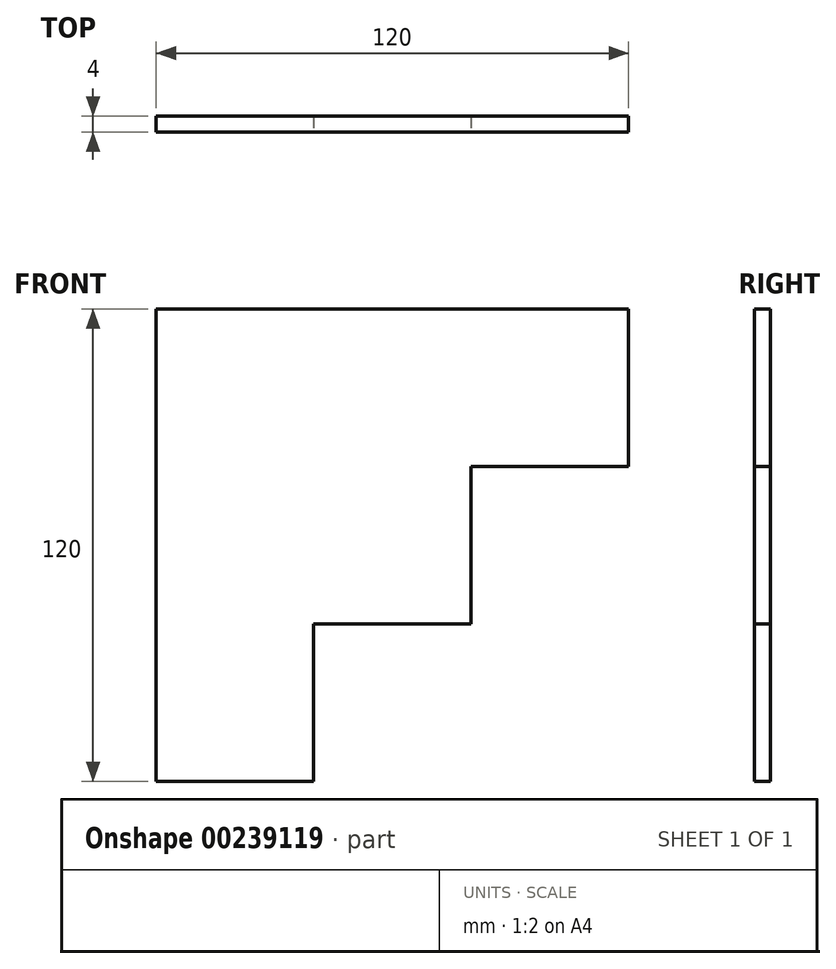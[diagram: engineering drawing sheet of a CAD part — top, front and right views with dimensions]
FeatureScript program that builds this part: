
annotation { "Feature Type Name" : "Feature", "Feature Type Description" : "" }
export const myFeature = defineFeature(function(context is Context, id is Id, definition is map)
    precondition{}
    {
        {
            assignVariable(context, id + "F0", {"name" : "v", "anyValue" : 4});
        }
        {
            var Q0;
            Q0=qCreatedBy(makeId("Front.planeOp"),FACE);
            var sketch = newSketch(context, id + "F1", { "sketchPlane" : qUnion([Q0])});
            skLineSegment(sketch, "E0.bottom", {"start": v(60, 60) * mm, "end": v(-60, 60) * mm});
            skLineSegment(sketch, "E0.top", {"start": v(60, -60) * mm, "end": v(-60, -60) * mm});
            skLineSegment(sketch, "E0.left", {"start": v(60, 60) * mm, "end": v(60, -60) * mm});
            skLineSegment(sketch, "E0.right", {"start": v(-60, 60) * mm, "end": v(-60, -60) * mm});
            skPoint(sketch, "E0.middle", {"position": v(0, 0) * mm});
            skSolve(sketch);
        }
        {
            var Q0;
            Q0 = qSketchRegion(id + "F1", true);
            extrude(context, id + "F2", {"entities" : qUnion([Q0]), "endBound" : BoundingType.SYMMETRIC, "depth" : (getVariable(context, 'v')) * mm});
        }
        {
            var Q0;
            Q0=makeQuery(id+"F2.opExtrude","CAP_FACE",FACE,{"disambiguationData":[OSD([sQuery(id+"F1.wireOp",EDGE,"E0.bottom"),sQuery(id+"F1.wireOp",EDGE,"E0.top"),sQuery(id+"F1.wireOp",EDGE,"E0.left"),sQuery(id+"F1.wireOp",EDGE,"E0.right")])],"isStart":false});
            var sketch = newSketch(context, id + "F3", { "sketchPlane" : qUnion([Q0])});
            skLineSegment(sketch, "E1.bottom", {"start": v(60, -60) * mm, "end": v(20, -60) * mm});
            skLineSegment(sketch, "E1.top", {"start": v(60, -20) * mm, "end": v(20, -20) * mm});
            skLineSegment(sketch, "E1.left", {"start": v(60, -60) * mm, "end": v(60, -20) * mm});
            skLineSegment(sketch, "E1.right", {"start": v(20, -60) * mm, "end": v(20, -20) * mm});
            skLineSegment(sketch, "E2.bottom", {"start": v(20, -20) * mm, "end": v(60, -20) * mm});
            skLineSegment(sketch, "E2.top", {"start": v(20, 20) * mm, "end": v(60, 20) * mm});
            skLineSegment(sketch, "E2.left", {"start": v(20, -20) * mm, "end": v(20, 20) * mm});
            skLineSegment(sketch, "E2.right", {"start": v(60, -20) * mm, "end": v(60, 20) * mm});
            skLineSegment(sketch, "E3.bottom", {"start": v(20, -20) * mm, "end": v(-20, -20) * mm});
            skLineSegment(sketch, "E3.top", {"start": v(20, -60) * mm, "end": v(-20, -60) * mm});
            skLineSegment(sketch, "E3.left", {"start": v(20, -20) * mm, "end": v(20, -60) * mm});
            skLineSegment(sketch, "E3.right", {"start": v(-20, -20) * mm, "end": v(-20, -60) * mm});
            skSolve(sketch);
        }
        {
            var Q0;
            Q0 = qSketchRegion(id + "F3", true);
            extrude(context, id + "F4", {"entities" : qUnion([Q0]), "operationType" : NewBodyOperationType.REMOVE, "endBound" : BoundingType.THROUGH_ALL, "oppositeDirection" : true, "depth" : 25 * mm});
        }
    });
